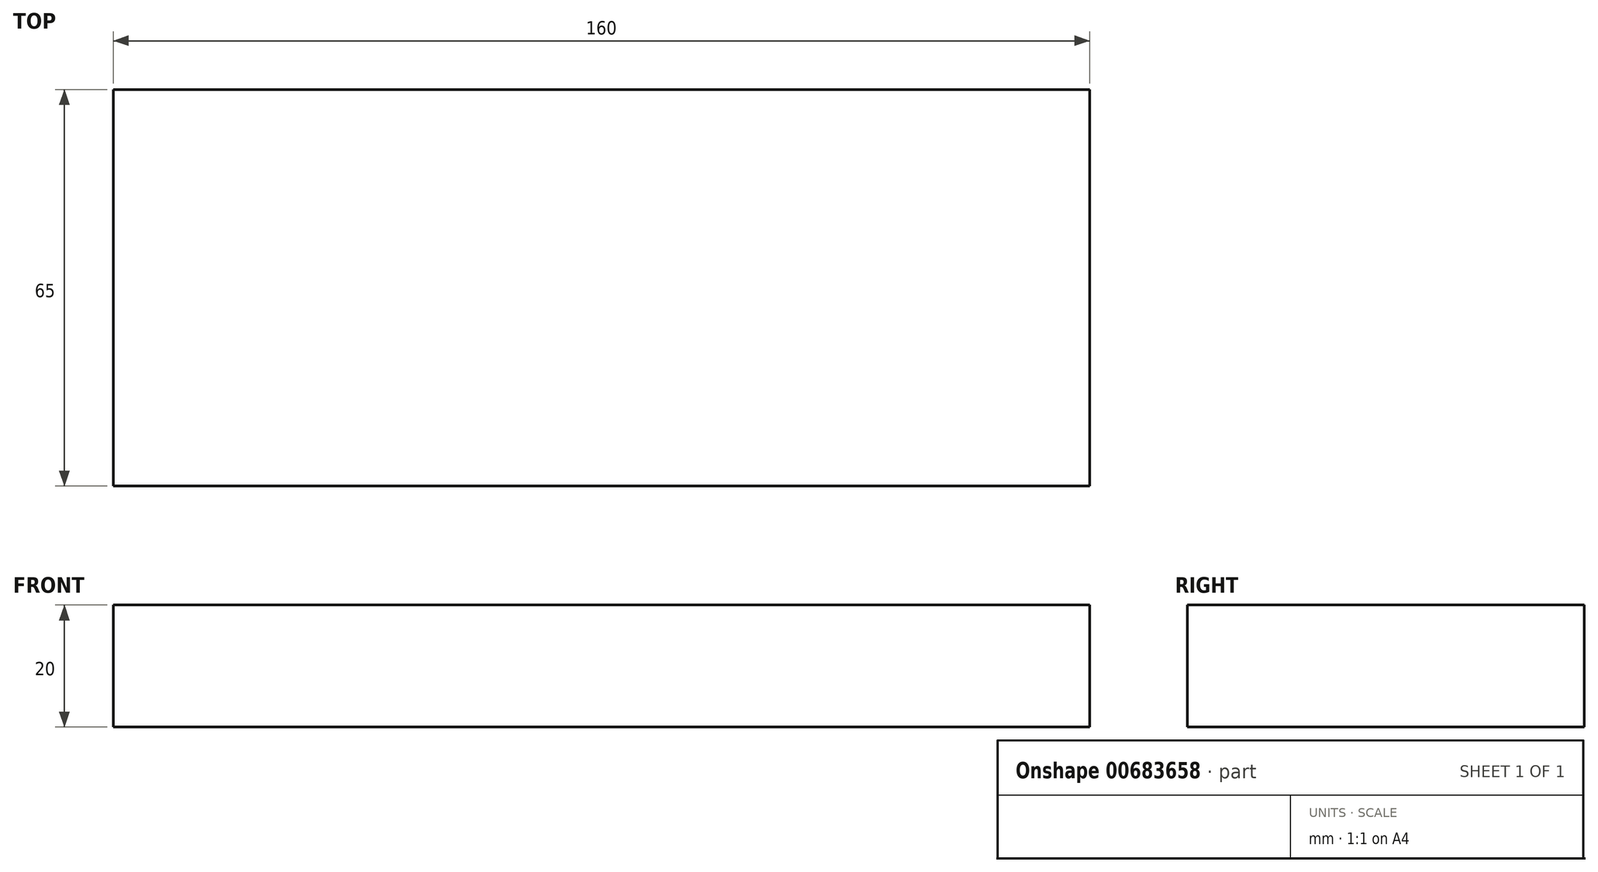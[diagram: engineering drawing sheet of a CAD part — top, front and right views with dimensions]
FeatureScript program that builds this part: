
annotation { "Feature Type Name" : "Feature", "Feature Type Description" : "" }
export const myFeature = defineFeature(function(context is Context, id is Id, definition is map)
    precondition{}
    {
        {
            var Q0;
            Q0=qCreatedBy(makeId("Top.planeOp"),FACE);
            var sketch = newSketch(context, id + "F0", { "sketchPlane" : qUnion([Q0])});
            skLineSegment(sketch, "E0.bottom", {"start": v(0, 0) * mm, "end": v(160, 0) * mm});
            skLineSegment(sketch, "E0.top", {"start": v(0, 65) * mm, "end": v(160, 65) * mm});
            skLineSegment(sketch, "E0.left", {"start": v(0, 0) * mm, "end": v(0, 65) * mm});
            skLineSegment(sketch, "E0.right", {"start": v(160, 0) * mm, "end": v(160, 65) * mm});
            skSolve(sketch);
        }
        {
            var Q0;
            Q0=makeQuery(id+"F0.imprint","IMPRINT",FACE,{"disambiguationData":[TD([[makeQuery(id+"F0.imprint","IMPRINT",EDGE,{"derivedFrom":sQuery(id+"F0.wireOp",EDGE,"E0.bottom")}),1.0]])]});
            extrude(context, id + "F1", {"entities" : qUnion([Q0]), "depth" : 20 * mm, "offsetDistance" : 25 * mm});
        }
    });
